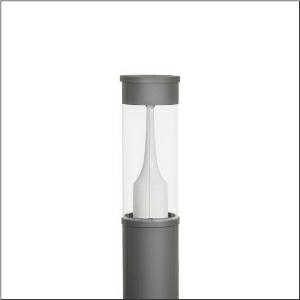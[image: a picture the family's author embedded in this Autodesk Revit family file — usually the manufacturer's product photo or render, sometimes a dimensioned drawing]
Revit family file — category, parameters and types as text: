
# Revit family: city-light_120_iq___p1_0a_5xa5285bf14h_8c15
name_source: partatom
category: Lighting Fixtures
units: mm (PartAtom-declared; Revit-internal decimal feet)

## family parameters
Cut with Voids When Loaded = No
Host = Face
Light Source = No
Part Type = Normal
Room Calculation Point = No
Round Connector Dimension = Use Diameter
Shared = No

## types (1)
- --- (1 x LED, 1510 lm, 12.9 W, 2200K)
    Apparent Load = 13 VA
    CIE Flux Codes = 32 61 90 93 100
    Color Rendering = 70
    Color Temperature = 2200K
    Default Elevation = 1800 mm
    Description = City-Light 120 iQ, bollard luminaire, Module 540 iQ-SR, primary light control with 3 zone facetted reflector, of plastic, silver coated, highly specular, structured, primary optical cover: cover, of PMMA, transparent, partly coated, light distribution: P1.0a, primary light characteristic: strongly asymmetric, LED, High Power LED, rated luminous flux: 1.510lm, luminous efficacy: 117lm/W, light colour: 722, colour temperature: 2200K, control gear: iQ Street-Remote, control: pre-setting: logarithmic dimming characteristic, Street-Remote, Auto-Match, Temp-Guard, Lumen-Switch, Night-Set, Smart-Wire, Light-Fading, Desk-Remote (wireless, voltage-free reading and setting of iQ features in the workshop via application-optimized NFC function/RFID function), optimised constant luminous flux control (CLO 2.0), with terminal, 6-pole, max. 2.5mm², mains connection: 230..240V, AC, 50/60Hz, start of lifetime: 13W, end of service life: 13W, reduction: 6W, luminaire housing, cylindrical, of extruded aluminium section, coated, Siteco® metallic grey (DB 702S), length: 1.200mm, diameter: 200mm, Module 540 iQ-SR, traffic white (RAL 9016), equipment: standard, protection rating (complete): IP54, insulation class (complete): insulation class II (safety insulation), certification: CE, ENEC, VDE, packaging unit: 1 piece

Light Distribution: P1.0a
    Height = 500 mm
    Lamp = 1 x LED
    Lamp Light Flux = 1510 lm
    Lamp Power = 12.9 W
    Lamp count = 1
    Length = 200 mm  [stored 0.656168 ft]
    Luminous efficacy = 117 lm/W
    Manufacturer = Siteco
    ModVariant = No
    Model = 5XA5285BF14H
    Mounting Place = Floor
    Mounting Type = Freestanding
    Number of Poles = 1
    OnlyDefault = Yes
    Power Factor = 1
    Product Name = City-Light 120 iQ | P1.0a
    Product group = bollard luminaire
    ProductGroupID = 1304
    Protection Class = Protection class II
    Protection Degree = IP 54
    RLX_Detail_Level = 1
    RLX_Emergency_Light_Flux = 0 lm
    RLX_Emergency_Type = 0
    RLX_Emergency_Type_DB = No
    RlxData = <blob elided: 52973 chars, md5=f4230a0a>
    Socket = socket
    Standby Power = 0 W
    System Light Flux = 1510 lm
    System Power = 13 W
    Type Comments = factory setting: luminous flux: 100 % | dim-lin: 254 | 516 mA
    Type Image = l_1006922.jpg
    URL = http://relux.com
    VarID = @adj_181093
    Voltage = 0 V
    Weight = 0.00 kg
    Width = 0 mm  [stored 0 ft]

note: [stored X ft] marks values corroborated as IEEE doubles in the binary element streams (Revit-internal decimal feet)

## geometry (parser evidence)
native form markers: Blend x4, Sweep x15
no freeform markers — native parametric forms only
